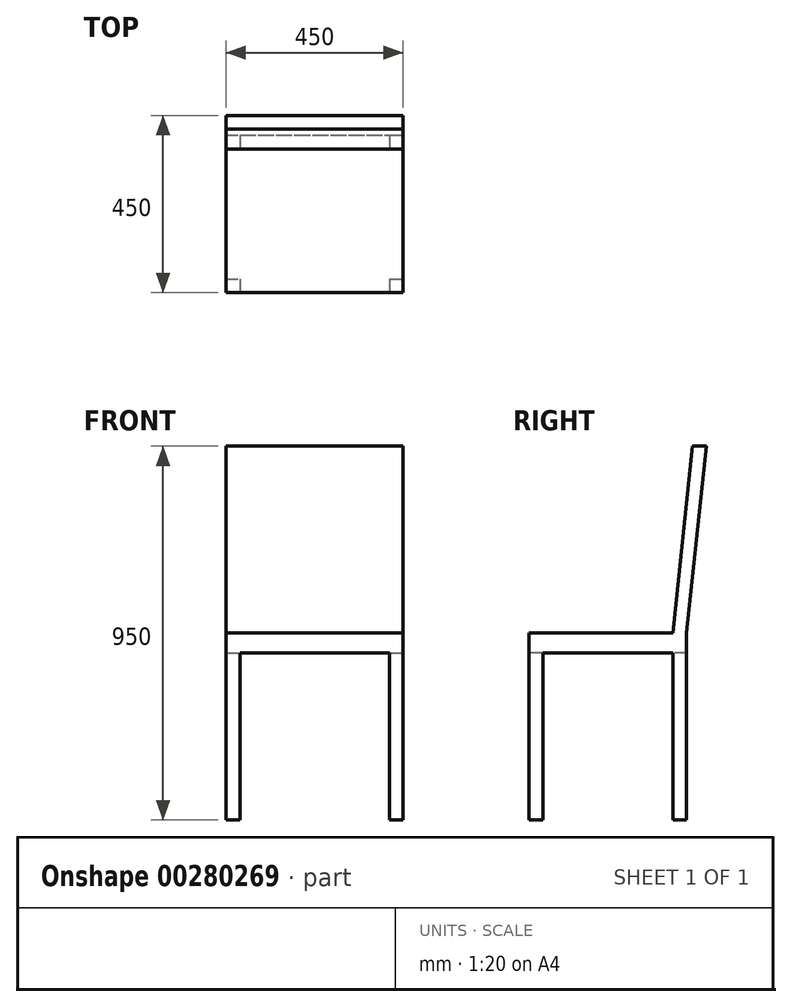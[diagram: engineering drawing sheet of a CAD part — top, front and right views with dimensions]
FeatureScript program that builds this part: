
annotation { "Feature Type Name" : "Feature", "Feature Type Description" : "" }
export const myFeature = defineFeature(function(context is Context, id is Id, definition is map)
    precondition{}
    {
        {
            var Q0;
            Q0=qCreatedBy(makeId("Top.planeOp"),FACE);
            var sketch = newSketch(context, id + "F0", { "sketchPlane" : qUnion([Q0])});
            skLineSegment(sketch, "E0.bottom", {"start": v(225, 225) * mm, "end": v(-225, 225) * mm});
            skLineSegment(sketch, "E0.top", {"start": v(225, -225) * mm, "end": v(-225, -225) * mm});
            skLineSegment(sketch, "E0.left", {"start": v(225, 225) * mm, "end": v(225, -225) * mm});
            skLineSegment(sketch, "E0.right", {"start": v(-225, 225) * mm, "end": v(-225, -225) * mm});
            skPoint(sketch, "E0.middle", {"position": v(0, 0) * mm});
            skSolve(sketch);
        }
        {
            var Q0;
            Q0=qSketchRegion(id+"F0",true);
            extrude(context, id + "F1", {"entities" : qUnion([Q0]), "depth" : 950 * mm});
        }
        {
            var Q0;
            Q0=makeQuery(id+"F1.opExtrude","SWEPT_FACE",FACE,{"disambiguationData":[OSD([sQuery(id+"F0.wireOp",EDGE,"E0.left")])]});
            var sketch = newSketch(context, id + "F2", { "sketchPlane" : qUnion([Q0])});
            skLineSegment(sketch, "E1.bottom", {"start": v(-225, 475) * mm, "end": v(225, 475) * mm});
            skLineSegment(sketch, "E1.top", {"start": v(-225, 425) * mm, "end": v(225, 425) * mm});
            skLineSegment(sketch, "E1.left", {"start": v(-225, 475) * mm, "end": v(-225, 425) * mm});
            skLineSegment(sketch, "E1.right", {"start": v(225, 475) * mm, "end": v(225, 425) * mm});
            skLineSegment(sketch, "E2", {"start": v(225, 950) * mm, "end": v(175, 475) * mm});
            skLineSegment(sketch, "E3", {"start": v(190, 950) * mm, "end": v(140, 475) * mm});
            skLineSegment(sketch, "E4", {"start": v(175, 475) * mm, "end": v(175, 0) * mm});
            skLineSegment(sketch, "E5", {"start": v(140, 475) * mm, "end": v(140, 0) * mm});
            skLineSegment(sketch, "E6.bottom", {"start": v(-225, 425) * mm, "end": v(-190, 425) * mm});
            skLineSegment(sketch, "E6.top", {"start": v(-225, 0) * mm, "end": v(-190, 0) * mm});
            skLineSegment(sketch, "E6.left", {"start": v(-225, 425) * mm, "end": v(-225, 0) * mm});
            skLineSegment(sketch, "E6.right", {"start": v(-190, 425) * mm, "end": v(-190, 0) * mm});
            skSolve(sketch);
        }
        {
            var Q0;
            {var subQ0=sQuery(id+"F2.wireOp",EDGE,"E1.right");Q0=makeQuery(id+"F2.imprint","IMPRINT",FACE,{"disambiguationData":[TD([[makeQuery(id+"F2.imprint","IMPRINT",EDGE,{"derivedFrom":subQ0}),-1.0]])]});}
            var Q1;
            {var subQ4=sQuery(id+"F2.wireOp",EDGE,"E3");Q1=makeQuery(id+"F2.imprint","IMPRINT",FACE,{"disambiguationData":[TD([[makeQuery(id+"F2.imprint","IMPRINT",EDGE,{"derivedFrom":subQ4}),-1.0]])]});}
            var Q2;
            {var subQ4=sQuery(id+"F2.wireOp",EDGE,"E2");Q2=makeQuery(id+"F2.imprint","IMPRINT",FACE,{"disambiguationData":[TD([[makeQuery(id+"F2.imprint","IMPRINT",EDGE,{"derivedFrom":subQ4}),1.0]])]});}
            var Q3;
            {var subQ0=sQuery(id+"F2.wireOp",EDGE,"E6.right");Q3=makeQuery(id+"F2.imprint","IMPRINT",FACE,{"disambiguationData":[TD([[makeQuery(id+"F2.imprint","IMPRINT",EDGE,{"derivedFrom":subQ0}),1.0]])]});}
            var Q4;
            {var subQ1=sQuery(id+"F0.wireOp",EDGE,"E0.left");var subQ4=sQuery(id+"F2.wireOp",EDGE,"E4");var subQ6=makeQuery(id+"F1.opExtrude","CAP_EDGE",EDGE,{"disambiguationData":[OSD([subQ1])],"isStart":true});var subQ7=makeQuery(id+"F2.imprint","INTERSECT",VERTEX,{"derivedFrom":[subQ6,subQ4]});Q4=makeQuery(id+"F2.imprint","IMPRINT",FACE,{"disambiguationData":[TD([[makeQuery(id+"F2.imprint","IMPRINT",EDGE,{"disambiguationData":[TD([[subQ7,1.0]])],"derivedFrom":subQ4}),1.0]])]});}
            extrude(context, id + "F3", {"entities" : qUnion([Q0, Q1, Q2, Q3, Q4]), "operationType" : NewBodyOperationType.REMOVE, "endBound" : BoundingType.THROUGH_ALL, "oppositeDirection" : true, "depth" : 25 * mm});
        }
        {
            var Q0;
            Q0=makeQuery(id+"F1.opExtrude","SWEPT_FACE",FACE,{"disambiguationData":[OSD([sQuery(id+"F0.wireOp",EDGE,"E0.top")])]});
            var sketch = newSketch(context, id + "F4", { "sketchPlane" : qUnion([Q0])});
            skLineSegment(sketch, "E7", {"start": v(-190, 0) * mm, "end": v(-190, 425) * mm});
            skLineSegment(sketch, "E8", {"start": v(-190, 425) * mm, "end": v(190, 425) * mm});
            skLineSegment(sketch, "E9", {"start": v(190, 0) * mm, "end": v(190, 425) * mm});
            skSolve(sketch);
        }
        {
            var Q0;
            Q0 = qSketchRegion(id + "F4", true);
            var Q1;
            {var subQ0=sQuery(id+"F4.wireOp",EDGE,"E7");Q1=makeQuery(id+"F4.imprint","IMPRINT",FACE,{"disambiguationData":[TD([[makeQuery(id+"F4.imprint","IMPRINT",EDGE,{"derivedFrom":subQ0}),-1.0]])]});}
            extrude(context, id + "F5", {"entities" : qUnion([Q0, Q1]), "operationType" : NewBodyOperationType.REMOVE, "endBound" : BoundingType.THROUGH_ALL, "oppositeDirection" : true, "depth" : 25 * mm});
        }
    });
